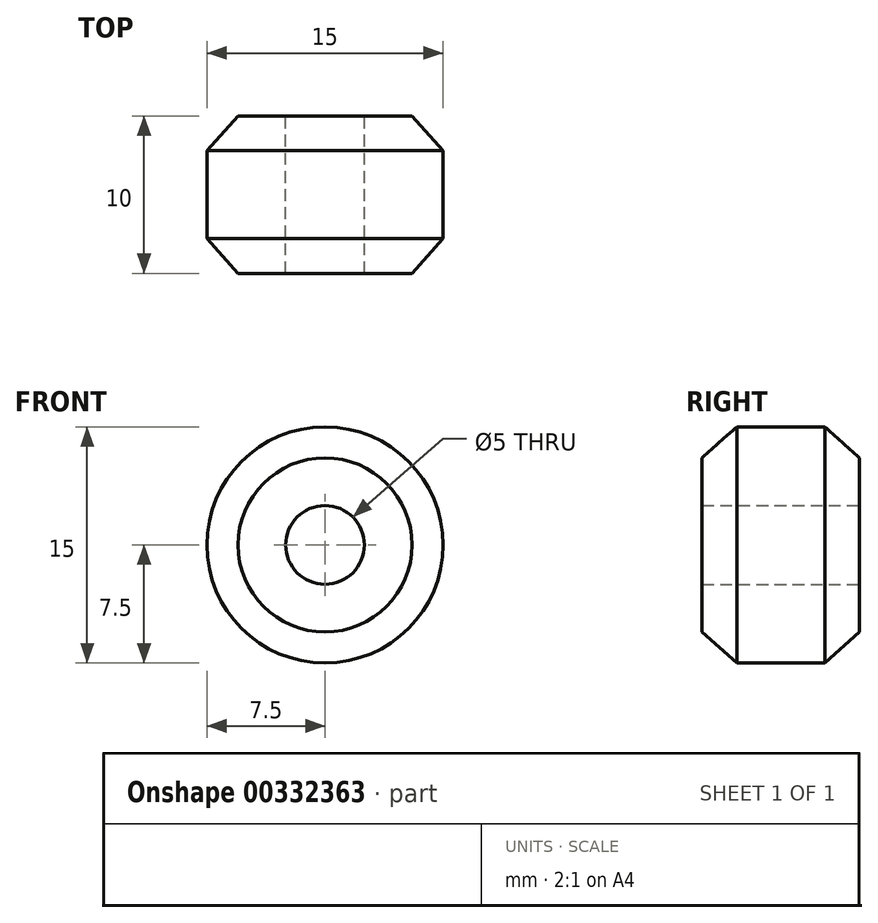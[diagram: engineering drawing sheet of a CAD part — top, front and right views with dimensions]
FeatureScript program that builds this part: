
annotation { "Feature Type Name" : "Feature", "Feature Type Description" : "" }
export const myFeature = defineFeature(function(context is Context, id is Id, definition is map)
    precondition{}
    {
        {
            var Q0;
            Q0=qCreatedBy(makeId("Top.planeOp"),FACE);
            var sketch = newSketch(context, id + "F0", { "sketchPlane" : qUnion([Q0])});
            skLineSegment(sketch, "E0", {"start": v(-2.5, 0) * mm, "end": v(-2.5, 5) * mm});
            skLineSegment(sketch, "E1", {"start": v(-2.5, 5) * mm, "end": v(-5.53, 5) * mm});
            skLineSegment(sketch, "E2", {"start": v(-5.53, 5) * mm, "end": v(-7.5, 2.8) * mm});
            skLineSegment(sketch, "E3", {"start": v(-7.5, 2.8) * mm, "end": v(-7.5, 0) * mm});
            skLineSegment(sketch, "E4.MirrorCS", {"start": v(-7.5, -2.8) * mm, "end": v(-7.5, 0) * mm});
            skLineSegment(sketch, "E5.MirrorCS", {"start": v(-2.5, -5) * mm, "end": v(-5.53, -5) * mm});
            skLineSegment(sketch, "E6.MirrorCS", {"start": v(-2.5, 0) * mm, "end": v(-2.5, -5) * mm});
            skLineSegment(sketch, "E7.MirrorCS", {"start": v(-5.53, -5) * mm, "end": v(-7.5, -2.8) * mm});
            skLineSegment(sketch, "E8", {"start": v(0, 0) * mm, "end": v(0, -3.68) * mm});
            skSolve(sketch);
        }
        {
            var Q0;
            Q0=makeQuery(id+"F0.imprint","IMPRINT",FACE,{"disambiguationData":[TD([[makeQuery(id+"F0.imprint","IMPRINT",EDGE,{"derivedFrom":sQuery(id+"F0.wireOp",EDGE,"E0")}),1.0]])]});
            var Q1;
            Q1=sQuery(id+"F0.wireOp",EDGE,"E8");
            revolve(context, id + "F1", {"surfaceOperationType" : NewSurfaceOperationType.NEW, "entities" : qUnion([Q0]), "axis" : qUnion([Q1]), "revolveType" : RevolveType.FULL});
        }
    });
